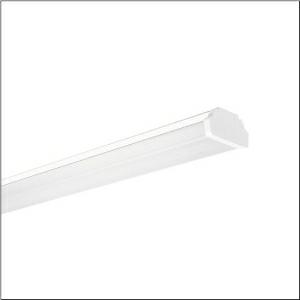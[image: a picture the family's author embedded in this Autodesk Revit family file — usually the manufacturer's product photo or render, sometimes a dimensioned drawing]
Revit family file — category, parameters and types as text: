
# Revit family: dus_r__31_gen_2_53bd812mv4fxd2_6b37
name_source: partatom
category: Lighting Fixtures
units: mm (PartAtom-declared; Revit-internal decimal feet)

## family parameters
Cut with Voids When Loaded = No
Host = Face
Light Source = No
Part Type = Normal
Room Calculation Point = No
Round Connector Dimension = Use Diameter
Shared = No

## types (1)
- --- (1 x LED, 15440 lm, 82.3 W, 4000K)
    Apparent Load = 82 VA
    CIE Flux Codes = 47 80 95 93 100
    Color Rendering = 80
    Color Temperature = 4000K
    Default Elevation = 1800 mm
    Description = DUS® 31 Gen.2, luminaire insert, of sheet steel, coil coated, white, length: 1.535mm, width: 81mm, height: 90mm, 5x system unit, system units: 307mm, LED rated luminous flux: 15.440lm, light colour: 840, control gear: ON/OFF Multilumen, control gear: ECG, with plug, 3-pole, with phase selection, mains connection: 220..240V, AC, 50/60Hz, rated input power: 82W, through-wiring accessed according to module size, primary optical cover: cover, of PMMA, light emission: direct distribution, primary light characteristic: symmetric, protection rating (complete): IP20, protection rating (LED compartment): IP50, insulation class (complete): insulation class I (protective earthing), certification: CE, ENEC, VDE, UKCA, impact resistance: IK03, permissible ambient temperature for indoor applications: -35..+35°C, corresponds to IFS (International Featured Standards) requirements for safety and quality in the food industry, reducing of maximum allowable ambient temperature of 5°C with ceiling mounting, packaging unit: 1 piece
    Height = 95 mm
    Lamp = 1 x LED
    Lamp Light Flux = 15440 lm
    Lamp Power = 82.3 W
    Lamp count = 1
    Length = 1535 mm
    Luminous efficacy = 188 lm/W
    Manufacturer = Siteco
    ModVariant = No
    Model = 53BD812MV4FXD2
    Mounting Place = Ceiling
    Mounting Type = Pendant
    Number of Poles = 1
    OnlyDefault = Yes
    Power Factor = 1
    Product Name = DUS® 31 Gen.2
    Product group = luminaire insert
    ProductGroupID = 902
    Protection Class = Protection class I
    Protection Degree = IP 20
    RLX_Detail_Level = 1
    RLX_Emergency_Light_Flux = 0 lm
    RLX_Emergency_Type = 0
    RLX_Emergency_Type_DB = No
    RlxData = <blob elided: 29701 chars, md5=478da1b4>
    Socket = socket
    Standby Power = 0 W
    System Light Flux = 15440 lm
    System Power = 82 W
    Type Comments = factory setting: luminous flux: 100 % | (A | C | E) | 193 mA
    Type Image = l_1319596.jpg
    URL = http://relux.com
    VarID = @adj_042276
    Voltage = 0 V
    Weight = 0.00 kg
    Width = 81 mm

## geometry (parser evidence)
native form markers: Blend x4, Sweep x13
no freeform markers — native parametric forms only
